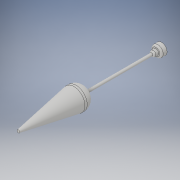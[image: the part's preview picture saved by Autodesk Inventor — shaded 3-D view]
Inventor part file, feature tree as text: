
AUTODESK INVENTOR PART (.ipt)
format: ipt  version: 2017 (Build 210142000, 142)  size: 151,040 bytes
history: native  units: in
note: dims shown in document units (in); Inventor stores cm internally (conversion verified against a paired STEP export)
features: extrude x5, sketch x4, fillet x2, other x2, thicken_offset x1, loft x1
ambient origin geometry x8: Origin, YZ Plane, XZ Plane, XY Plane, X Axis, Y Axis, Z Axis, Center Point
bodies: Solid1 (feature_tree)
feature tree (15):
  sketch  "Sketch1"  dims[d0=0.5in d1=0.25in]
  extrude  "Extrusion1"  Depth=0.25in
  extrude  "Extrusion2"  Depth=0.45in TaperAngle=0.0deg
  extrude  "Extrusion3"  Depth=3.0in TaperAngle=0.0deg
  extrude  "Extrusion6"  Depth=3.0in TaperAngle=0.0deg
  fillet  "Fillet3"  Radius=0.4in
  thicken_offset  "Thicken1"
  extrude  "Extrusion13"  Depth=2.5in
  loft  "Loft1"
  fillet  "Fillet5"  Radius=2.5in
  sketch  "Sketch2"  dims[d2=0.25in d3=0.0in d4=0.45in d5=0.0in]
  sketch  "Sketch5"  dims[d7=0.125in d8=3.0in d9=0.0in]
  sketch  "Sketch14"  dims[d16=1.0in d17=3.0in d18=0.0in d19=0.4in d20=2.5in d21=2.5in d41=2.5in d42=0.0in d43=0.0in d44=90.0deg d45=0.0in d46=90.0deg d47=0.075in]
  other  "Edges1"
  other  "Edges2"
